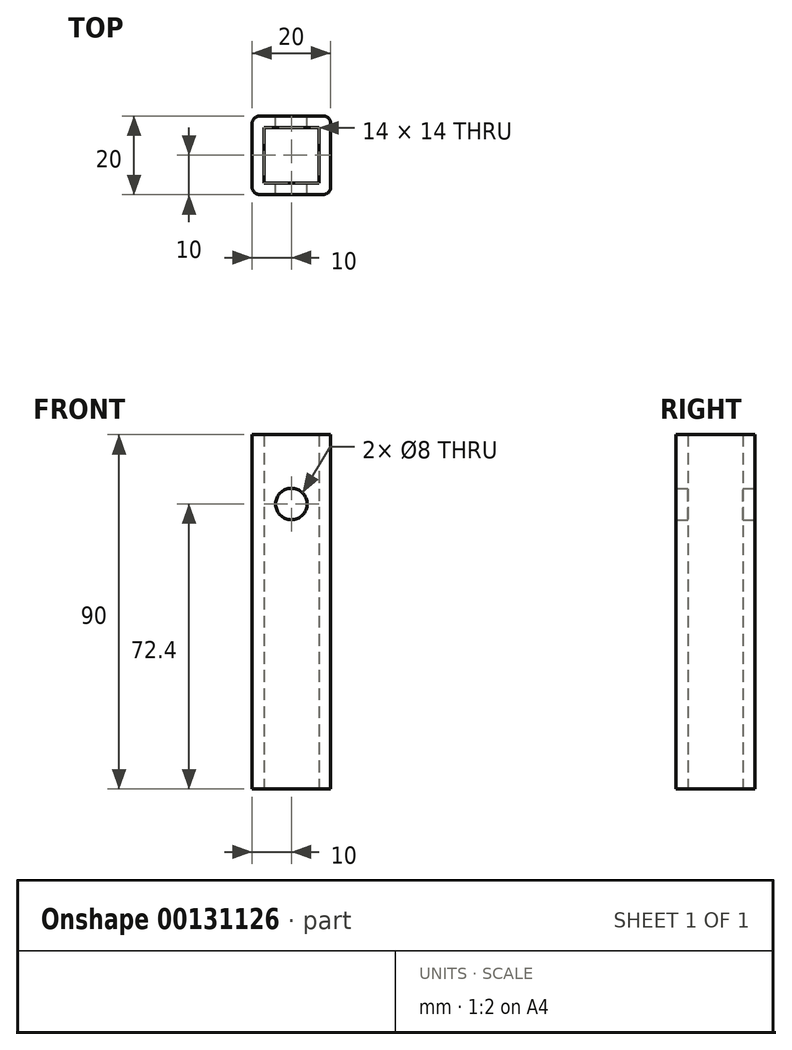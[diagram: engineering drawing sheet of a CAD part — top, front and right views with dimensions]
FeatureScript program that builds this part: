
annotation { "Feature Type Name" : "Feature", "Feature Type Description" : "" }
export const myFeature = defineFeature(function(context is Context, id is Id, definition is map)
    precondition{}
    {
        {
            var Q0;
            Q0=qCreatedBy(makeId("Top.planeOp"),FACE);
            var sketch = newSketch(context, id + "F0", { "sketchPlane" : qUnion([Q0])});
            skLineSegment(sketch, "E0.bottom", {"start": v(10, -10) * mm, "end": v(-10, -10) * mm});
            skLineSegment(sketch, "E0.top", {"start": v(10, 10) * mm, "end": v(-10, 10) * mm});
            skLineSegment(sketch, "E0.left", {"start": v(10, -10) * mm, "end": v(10, 10) * mm});
            skLineSegment(sketch, "E0.right", {"start": v(-10, -10) * mm, "end": v(-10, 10) * mm});
            skPoint(sketch, "E0.middle", {"position": v(0, 0) * mm});
            skLineSegment(sketch, "E1.bottom", {"start": v(7, -7) * mm, "end": v(-7, -7) * mm});
            skLineSegment(sketch, "E1.top", {"start": v(7, 7) * mm, "end": v(-7, 7) * mm});
            skLineSegment(sketch, "E1.left", {"start": v(7, -7) * mm, "end": v(7, 7) * mm});
            skLineSegment(sketch, "E1.right", {"start": v(-7, -7) * mm, "end": v(-7, 7) * mm});
            skSolve(sketch);
        }
        {
            var Q0;
            Q0=makeQuery(id+"F0.imprint","IMPRINT",FACE,{"disambiguationData":[TD([[makeQuery(id+"F0.imprint","IMPRINT",EDGE,{"derivedFrom":sQuery(id+"F0.wireOp",EDGE,"E0.bottom")}),-1.0]])]});
            extrude(context, id + "F1", {"entities" : qUnion([Q0]), "depth" : 90 * mm});
        }
        {
            var Q0;
            Q0=makeQuery(id+"F1.opExtrude","SWEPT_EDGE",EDGE,{"disambiguationData":[OSD([sQuery(id+"F0.wireOp",EDGE,"E0.bottom"),sQuery(id+"F0.wireOp",EDGE,"E0.left")])]});
            var Q1;
            Q1=makeQuery(id+"F1.opExtrude","SWEPT_EDGE",EDGE,{"disambiguationData":[OSD([sQuery(id+"F0.wireOp",EDGE,"E0.top"),sQuery(id+"F0.wireOp",EDGE,"E0.left")])]});
            var Q2;
            Q2=makeQuery(id+"F1.opExtrude","SWEPT_EDGE",EDGE,{"disambiguationData":[OSD([sQuery(id+"F0.wireOp",EDGE,"E0.bottom"),sQuery(id+"F0.wireOp",EDGE,"E0.right")])]});
            var Q3;
            Q3=makeQuery(id+"F1.opExtrude","SWEPT_EDGE",EDGE,{"disambiguationData":[OSD([sQuery(id+"F0.wireOp",EDGE,"E0.top"),sQuery(id+"F0.wireOp",EDGE,"E0.right")])]});
            fillet(context, id + "F2", {"entities" : qUnion([Q0, Q1, Q2, Q3]), "radius" : 2 * mm, "tangentPropagation" : true, "allowEdgeOverflow" : false});
        }
        {
            var Q0;
            Q0=makeQuery(id+"F1.opExtrude","SWEPT_FACE",FACE,{"disambiguationData":[OSD([sQuery(id+"F0.wireOp",EDGE,"E0.top")])]});
            var sketch = newSketch(context, id + "F3", { "sketchPlane" : qUnion([Q0])});
            skPoint(sketch, "E2", {"position": v(0, 72.4) * mm});
            skSolve(sketch);
        }
        {
            var Q0;
            Q0=sQuery(id+"F3.wireOp",VERTEX,"E2");
            var Q1;
            Q1=makeQuery(id+"F1.opExtrude","SWEPT_BODY",BODY,{"disambiguationData":[OSD([sQuery(id+"F0.wireOp",EDGE,"E0.bottom"),sQuery(id+"F0.wireOp",EDGE,"E0.top"),sQuery(id+"F0.wireOp",EDGE,"E0.left"),sQuery(id+"F0.wireOp",EDGE,"E0.right"),sQuery(id+"F0.wireOp",EDGE,"E1.bottom"),sQuery(id+"F0.wireOp",EDGE,"E1.top"),sQuery(id+"F0.wireOp",EDGE,"E1.left"),sQuery(id+"F0.wireOp",EDGE,"E1.right")])]});
            hole(context, id + "F4", {"style" : HoleStyle.SIMPLE, "endStyle" : HoleEndStyle.THROUGH, "holeDiameter" : 8 * mm, "locations" : qUnion([Q0]), "scope" : qUnion([Q1]), "isTappedThrough" : true});
        }
    });
